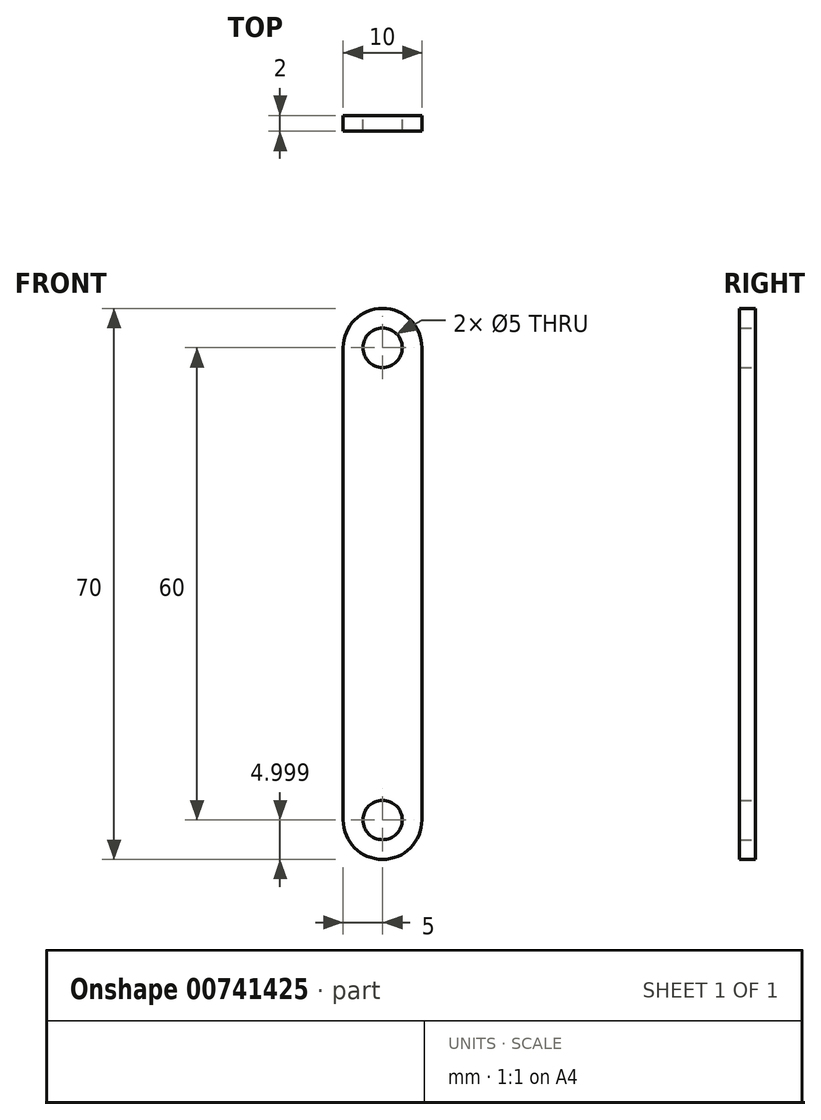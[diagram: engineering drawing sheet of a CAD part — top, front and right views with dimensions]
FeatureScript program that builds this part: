
annotation { "Feature Type Name" : "Feature", "Feature Type Description" : "" }
export const myFeature = defineFeature(function(context is Context, id is Id, definition is map)
    precondition{}
    {
        {
            var Q0;
            Q0=qCreatedBy(makeId("Front.planeOp"),FACE);
            var sketch = newSketch(context, id + "F0", { "sketchPlane" : qUnion([Q0])});
            skCircle(sketch, "E0", {"center": v(0, 42.93) * mm, "radius": 2.5 * mm});
            skCircle(sketch, "E1", {"center": v(0, -17.07) * mm, "radius": 2.5 * mm});
            skArc(sketch, "E2", {"start": v(5, 42.93) * mm, "mid": v(0, 47.93) * mm, "end": v(-5, 42.93) * mm});
            skArc(sketch, "E3", {"start": v(-5, -17.07) * mm, "mid": v(0, -22.07) * mm, "end": v(5, -17.07) * mm});
            skLineSegment(sketch, "E4", {"start": v(-5, 42.93) * mm, "end": v(-5, -17.07) * mm});
            skLineSegment(sketch, "E5", {"start": v(5, 42.93) * mm, "end": v(5, -17.07) * mm});
            skSolve(sketch);
        }
        {
            var Q0;
            Q0 = qSketchRegion(id + "F0", true);
            extrude(context, id + "F1", {"entities" : qUnion([Q0]), "depth" : 2 * mm, "offsetDistance" : 25.4 * mm});
        }
    });
